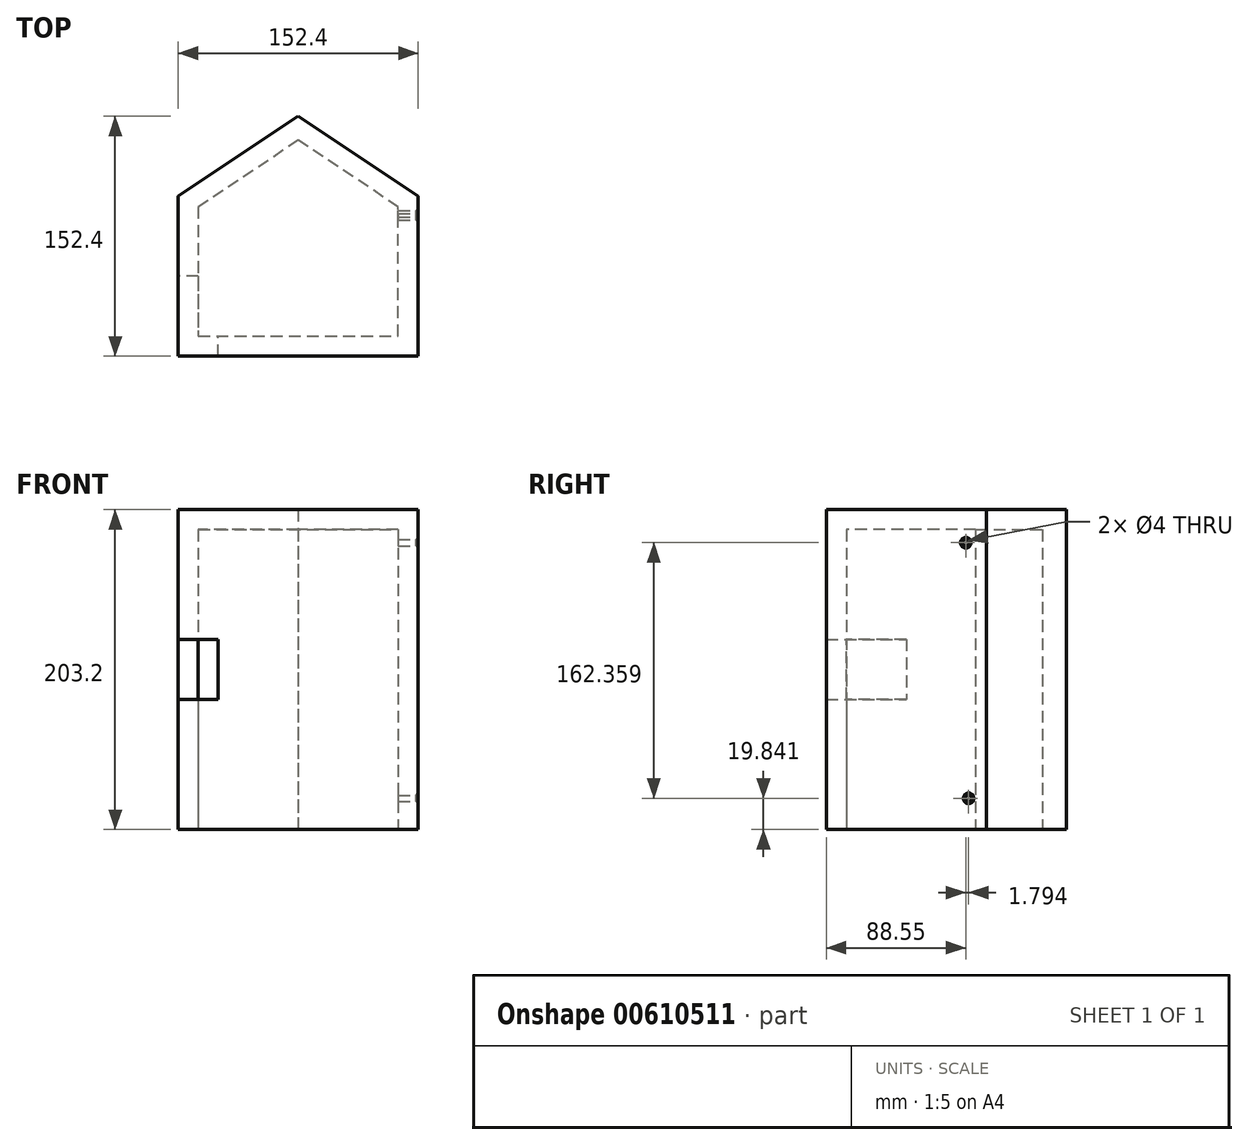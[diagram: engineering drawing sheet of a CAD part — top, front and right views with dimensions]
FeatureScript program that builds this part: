
annotation { "Feature Type Name" : "Feature", "Feature Type Description" : "" }
export const myFeature = defineFeature(function(context is Context, id is Id, definition is map)
    precondition{}
    {
        {
            var Q0;
            Q0=qCreatedBy(makeId("Top.planeOp"),FACE);
            var sketch = newSketch(context, id + "F0", { "sketchPlane" : qUnion([Q0])});
            skLineSegment(sketch, "E0", {"start": v(0, 0) * mm, "end": v(152.4, 0) * mm});
            skLineSegment(sketch, "E1", {"start": v(152.4, 0) * mm, "end": v(152.4, 101.6) * mm});
            skLineSegment(sketch, "E2", {"start": v(152.4, 101.6) * mm, "end": v(76.2, 152.4) * mm});
            skLineSegment(sketch, "E3", {"start": v(76.2, 152.4) * mm, "end": v(0, 101.6) * mm});
            skLineSegment(sketch, "E4", {"start": v(0, 101.6) * mm, "end": v(0, 0) * mm});
            skLineSegment(sketch, "E5", {"start": v(76.2, 152.4) * mm, "end": v(76.2, 0) * mm, "construction": true});
            skSolve(sketch);
        }
        {
            var Q0;
            Q0 = qSketchRegion(id + "F0", true);
            extrude(context, id + "F1", {"entities" : qUnion([Q0]), "endBound" : BoundingType.SYMMETRIC, "depth" : 203.2 * mm, "offsetDistance" : 25.4 * mm});
        }
        {
            var Q0;
            Q0=makeQuery(id+"F1.opExtrude","SWEPT_FACE",FACE,{"disambiguationData":[OSD([sQuery(id+"F0.wireOp",EDGE,"E4")])]});
            var sketch = newSketch(context, id + "F2", { "sketchPlane" : qUnion([Q0])});
            skLineSegment(sketch, "E6.bottom", {"start": v(0, 19.2) * mm, "end": v(-50.8, 19.2) * mm});
            skLineSegment(sketch, "E6.top", {"start": v(0, -18.9) * mm, "end": v(-50.8, -18.9) * mm});
            skLineSegment(sketch, "E6.left", {"start": v(0, 19.2) * mm, "end": v(0, -18.9) * mm});
            skLineSegment(sketch, "E6.right", {"start": v(-50.8, 19.2) * mm, "end": v(-50.8, -18.9) * mm});
            skSolve(sketch);
        }
        {
            var Q0;
            Q0=makeQuery(id+"F1.opExtrude","CAP_FACE",FACE,{"disambiguationData":[OSD([sQuery(id+"F0.wireOp",EDGE,"E0"),sQuery(id+"F0.wireOp",EDGE,"E1"),sQuery(id+"F0.wireOp",EDGE,"E2"),sQuery(id+"F0.wireOp",EDGE,"E3"),sQuery(id+"F0.wireOp",EDGE,"E4")])],"isStart":true});
            shell(context, id + "F3", {"entities" : qUnion([Q0]), "thickness" : 12.7 * mm});
        }
        {
            var Q0;
            Q0=makeQuery(id+"F2.imprint","IMPRINT",FACE,{"disambiguationData":[TD([[makeQuery(id+"F2.imprint","IMPRINT",EDGE,{"derivedFrom":sQuery(id+"F2.wireOp",EDGE,"E6.bottom")}),1.0]])]});
            var Q1;
            Q1 = qSketchRegion(id + "F2", true);
            extrude(context, id + "F4", {"entities" : qUnion([Q0, Q1]), "operationType" : NewBodyOperationType.REMOVE, "oppositeDirection" : true, "depth" : 25.4 * mm, "offsetDistance" : 25.4 * mm});
        }
        {
            var Q0;
            Q0=makeQuery(id+"F1.opExtrude","SWEPT_FACE",FACE,{"disambiguationData":[OSD([sQuery(id+"F0.wireOp",EDGE,"E1")])]});
            var sketch = newSketch(context, id + "F5", { "sketchPlane" : qUnion([Q0])});
            skCircle(sketch, "E7", {"center": v(20.32, 0) * mm, "radius": 10.16 * mm});
            skSolve(sketch);
        }
        {
            var Q0;
            Q0=makeQuery(id+"F1.opExtrude","SWEPT_FACE",FACE,{"disambiguationData":[OSD([sQuery(id+"F0.wireOp",EDGE,"E1")])]});
            var sketch = newSketch(context, id + "F6", { "sketchPlane" : qUnion([Q0])});
            skPoint(sketch, "E8", {"position": v(88.55, 80.6) * mm});
            skPoint(sketch, "E9", {"position": v(90.34, -81.76) * mm});
            skSolve(sketch);
        }
        {
            var Q0;
            Q0=sQuery(id+"F6.wireOp",VERTEX,"E8");
            var Q1;
            Q1=sQuery(id+"F6.wireOp",VERTEX,"E9");
            var Q2;
            Q2=makeQuery(id+"F1.opExtrude","SWEPT_BODY",BODY,{"disambiguationData":[OSD([sQuery(id+"F0.wireOp",EDGE,"E0"),sQuery(id+"F0.wireOp",EDGE,"E1"),sQuery(id+"F0.wireOp",EDGE,"E2"),sQuery(id+"F0.wireOp",EDGE,"E3"),sQuery(id+"F0.wireOp",EDGE,"E4")])]});
            hole(context, id + "F7", {"style" : HoleStyle.C_SINK, "endStyle" : HoleEndStyle.BLIND, "standardTappedOrClearance" : lookupTablePath({ "standard" : "ISO", "size" : "4", "type" : "Drilled" }), "standardBlindInLast" : lookupTablePath({ "standard" : "ISO", "size" : "4", "type" : "Drilled" }), "holeDiameter" : 4 * mm, "cSinkDiameter" : 6.72 * mm, "cSinkAngle" : 90 * degree, "majorDiameter" : 3 * mm, "holeDepth" : 14.2 * mm, "isTappedThrough" : true, "tappedDepth" : 12.7 * mm, "tapClearance" : 3, "locations" : qUnion([Q0, Q1]), "scope" : qUnion([Q2])});
        }
        {
            var Q0;
            Q0=makeQuery(id+"F1.opExtrude","CAP_EDGE",EDGE,{"disambiguationData":[OSD([sQuery(id+"F0.wireOp",EDGE,"E4")])],"isStart":true});
            var Q1;
            Q1=makeQuery(id+"F1.opExtrude","CAP_VERTEX",VERTEX,{"disambiguationData":[OSD([sQuery(id+"F0.wireOp",EDGE,"E3"),sQuery(id+"F0.wireOp",EDGE,"E4")])],"isStart":true});
            cPlane(context, id + "F8", {"entities" : qUnion([Q0, Q1]), "cplaneType" : CPlaneType.LINE_POINT, "offset" : 25.4 * mm, "width" : 152.4 * mm, "height" : 152.4 * mm});
        }
        {
            var Q0;
            Q0=makeQuery(id+"F1.opExtrude","CAP_FACE",FACE,{"disambiguationData":[OSD([sQuery(id+"F0.wireOp",EDGE,"E0"),sQuery(id+"F0.wireOp",EDGE,"E1"),sQuery(id+"F0.wireOp",EDGE,"E2"),sQuery(id+"F0.wireOp",EDGE,"E3"),sQuery(id+"F0.wireOp",EDGE,"E4")])],"isStart":true});
            cPlane(context, id + "F9", {"entities" : qUnion([Q0]), "cplaneType" : CPlaneType.OFFSET, "offset" : 0 * mm, "width" : 152.4 * mm, "height" : 152.4 * mm});
        }
    });
